# Revit family: Punto de acceso Wi-Fi
name_source: partatom
category: Equipement spécialisé
units: mm (PartAtom-declared; Revit-internal decimal feet)

## family parameters
Basée sur le plan de construction = Non
Cote de connecteur circulaire = Utiliser le diamètre
Couper avec des vides une fois chargée = Non
Partagée = Oui
Point de calcul de pièce = Non
Toujours verticalement = Oui
Type d'élément = Normal

## types (1)
- Punto de acceso Wi-Fi PoE
    Alcance en campo abierto = 80 mm  [stored 0.262467 ft]
    Alcance en interiores = 20 mm  [stored 0.0656168 ft]
    Altura (mm) = 66 mm  [stored 0.216535 ft]
    Anchura (mm) = 66 mm  [stored 0.216535 ft]
    Bridge función = Oui
    CGU = https://export.legrand.com
    Cifrado = WPA2
    Clasificación ETIM = EC000816
    Color = Blanco
    E-catalogo enlace = https://www.legrand.fr
    EAN = 3414972013277
    Elévation par défaut = 0 mm  [stored 0 ft]
    Fabricant = LEGRAND
    Formulación BIM = Punto de acceso Wi-Fi PoE
    Función = Legrand Wireless
    Gama de frecuencias (Mhz) = 2400
    Humedad = +95% max.
    IK = IK04
    IP = IP2X
    Numero RAL = 9003
    Número de pieza Legrand = 033523
    Número de usuarios = 16
    Potencia = 20 dBm - 10 mW max
    Profundidad (mm) = 44 mm  [stored 0.144357 ft]
    Seguridad = 802.11i
    Temperatura de almacenamiento = -20°C - 70°C
    Temperatura operativa = -5°C - 40°C

note: [stored X ft] marks values corroborated as IEEE doubles in the binary element streams (Revit-internal decimal feet)
